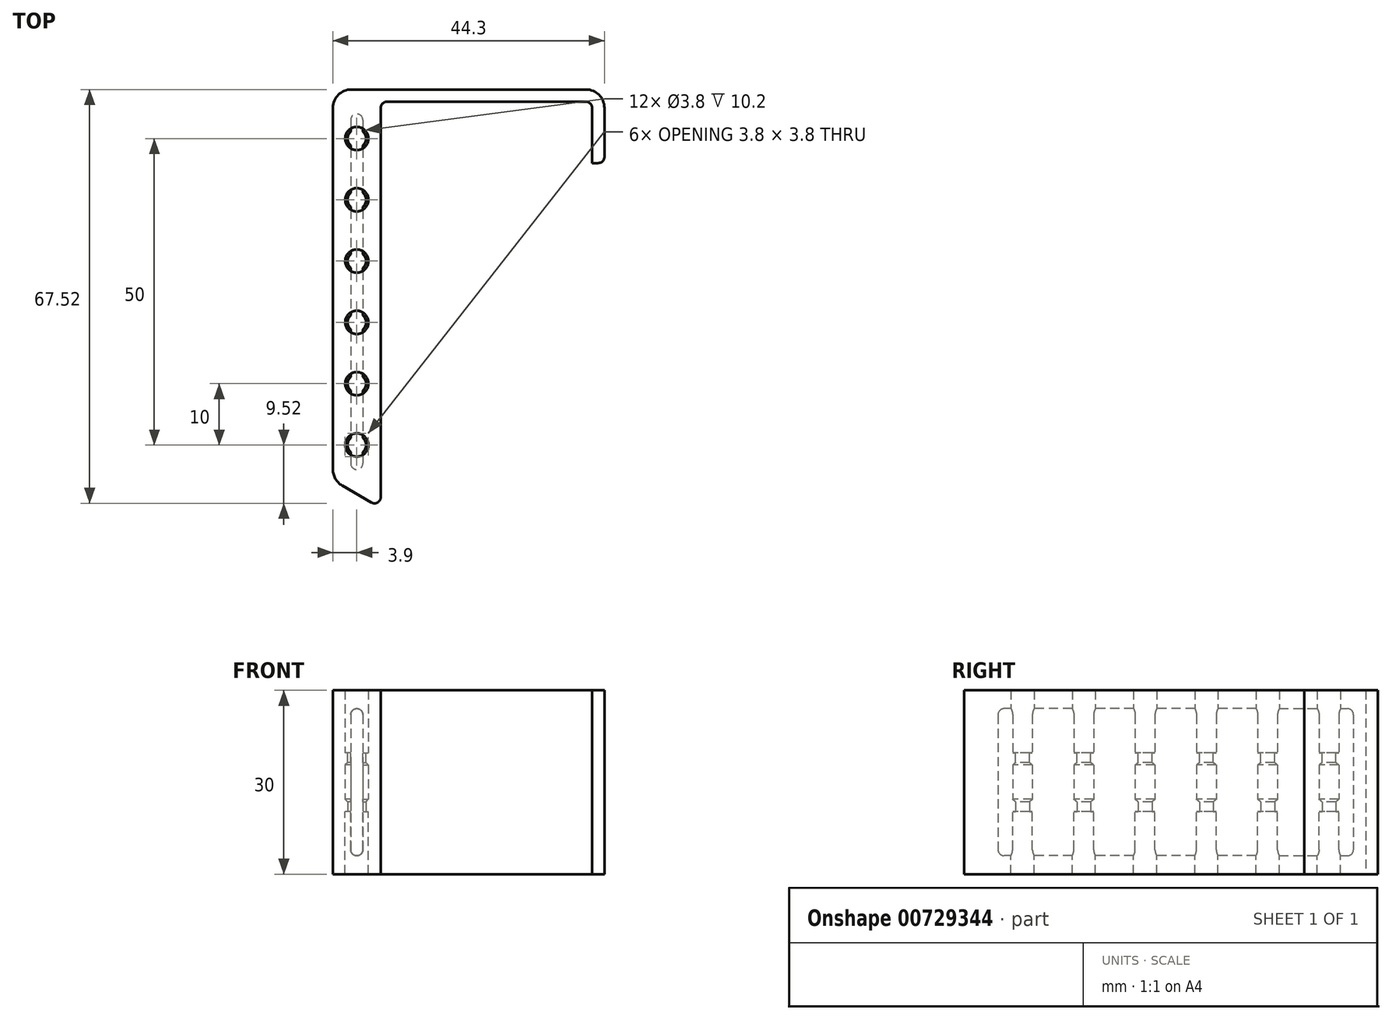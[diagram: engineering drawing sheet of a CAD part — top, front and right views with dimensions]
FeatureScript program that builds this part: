
annotation { "Feature Type Name" : "Feature", "Feature Type Description" : "" }
export const myFeature = defineFeature(function(context is Context, id is Id, definition is map)
    precondition{}
    {
        {
            var Q0;
            Q0=qCreatedBy(makeId("Top.planeOp"),FACE);
            var sketch = newSketch(context, id + "F0", { "sketchPlane" : qUnion([Q0])});
            skLineSegment(sketch, "E0", {"start": v(0, 0) * mm, "end": v(34.5, 0) * mm});
            skLineSegment(sketch, "E1", {"start": v(34.5, 0) * mm, "end": v(34.5, -10) * mm});
            skLineSegment(sketch, "E2", {"start": v(34.5, -10) * mm, "end": v(36.5, -10) * mm});
            skLineSegment(sketch, "E3", {"start": v(36.5, -10) * mm, "end": v(36.5, 2) * mm});
            skLineSegment(sketch, "E4", {"start": v(36.5, 2) * mm, "end": v(-2, 2) * mm});
            skLineSegment(sketch, "E5", {"start": v(0, 0) * mm, "end": v(0, 2) * mm, "construction": true});
            skLineSegment(sketch, "E6", {"start": v(0, 0) * mm, "end": v(-2, 0) * mm, "construction": true});
            skLineSegment(sketch, "E7", {"start": v(0, 0) * mm, "end": v(-2, 2) * mm});
            skLineSegment(sketch, "E8", {"start": v(-2, 0) * mm, "end": v(-2, 2) * mm, "construction": true});
            skSolve(sketch);
        }
        {
            var Q0;
            Q0 = qSketchRegion(id + "F0", true);
            extrude(context, id + "F1", {"entities" : qUnion([Q0]), "depth" : 15 * mm, "offsetDistance" : 25 * mm});
        }
        {
            var Q0;
            Q0=qCreatedBy(makeId("Top.planeOp"),FACE);
            var sketch = newSketch(context, id + "F2", { "sketchPlane" : qUnion([Q0])});
            skLineSegment(sketch, "E9", {"start": v(-2, 2) * mm, "end": v(-7.8, 2) * mm});
            skLineSegment(sketch, "E10", {"start": v(-7.8, 2) * mm, "end": v(-7.8, -61.75) * mm});
            skLineSegment(sketch, "E11", {"start": v(-7.8, -61.75) * mm, "end": v(0, -66.25) * mm});
            skLineSegment(sketch, "E12", {"start": v(0, -66.25) * mm, "end": v(0, 0) * mm});
            skLineSegment(sketch, "E13", {"start": v(-3.9, 2) * mm, "end": v(-3.9, -6) * mm, "construction": true});
            skLineSegment(sketch, "E14", {"start": v(-3.9, -6) * mm, "end": v(-3.9, -16) * mm, "construction": true});
            skLineSegment(sketch, "E15", {"start": v(-3.9, -16) * mm, "end": v(-3.9, -26) * mm, "construction": true});
            skLineSegment(sketch, "E16", {"start": v(-3.9, -26) * mm, "end": v(-3.9, -36) * mm, "construction": true});
            skLineSegment(sketch, "E17", {"start": v(-3.9, -36) * mm, "end": v(-3.9, -46) * mm, "construction": true});
            skLineSegment(sketch, "E18", {"start": v(-3.9, -46) * mm, "end": v(-3.9, -56) * mm, "construction": true});
            skLineSegment(sketch, "E19", {"start": v(-3.9, -56) * mm, "end": v(-3.9, -64) * mm, "construction": true});
            skCircle(sketch, "E20", {"center": v(-3.9, -6) * mm, "radius": 1.9 * mm});
            skCircle(sketch, "E21", {"center": v(-3.9, -16) * mm, "radius": 1.9 * mm});
            skCircle(sketch, "E22", {"center": v(-3.9, -26) * mm, "radius": 1.9 * mm});
            skCircle(sketch, "E23", {"center": v(-3.9, -36) * mm, "radius": 1.9 * mm});
            skCircle(sketch, "E24", {"center": v(-3.9, -46) * mm, "radius": 1.9 * mm});
            skCircle(sketch, "E25", {"center": v(-3.9, -56) * mm, "radius": 1.9 * mm});
            skLineSegment(sketch, "E26", {"start": v(-2, -56) * mm, "end": v(0, -56) * mm, "construction": true});
            skLineSegment(sketch, "E27", {"start": v(-5.8, -56) * mm, "end": v(-7.8, -56) * mm, "construction": true});
            skLineSegment(sketch, "E28", {"start": v(-2, 2) * mm, "end": v(0, 0) * mm});
            skPoint(sketch, "E29.orphan", {"position": v(0, 2) * mm});
            skSolve(sketch);
        }
        {
            var Q0;
            Q0 = qSketchRegion(id + "F2", true);
            var Q1;
            Q1=makeQuery(id+"F1.opExtrude","CAP_FACE",FACE,{"disambiguationData":[OSD([sQuery(id+"F0.wireOp",EDGE,"E0"),sQuery(id+"F0.wireOp",EDGE,"E1"),sQuery(id+"F0.wireOp",EDGE,"E2"),sQuery(id+"F0.wireOp",EDGE,"E3"),sQuery(id+"F0.wireOp",EDGE,"E4"),sQuery(id+"F0.wireOp",EDGE,"YZuL8Zb7-Wqwv-IhHu-uYE8-zltIC9lL77bN"),sQuery(id+"F0.wireOp",EDGE,"ZwzGtUW0-Jcxg-k5Jw-SNz7-18NdNkJmYsfR"),sQuery(id+"F0.wireOp",EDGE,"XFt9ytuQ-fa2W-s6oK-lxsI-mpyMaxMMDPJW")])],"isStart":false});
            extrude(context, id + "F3", {"entities" : qUnion([Q0]), "operationType" : NewBodyOperationType.ADD, "endBound" : BoundingType.UP_TO_SURFACE, "depth" : 25 * mm, "endBoundEntityFace" : qUnion([Q1]), "offsetDistance" : 25 * mm});
        }
        {
            var Q0;
            Q0=makeQuery(id+"F1.opExtrude","SWEPT_EDGE",EDGE,{"disambiguationData":[OSD([sQuery(id+"F0.wireOp",EDGE,"E0"),sQuery(id+"F0.wireOp",EDGE,"ZwzGtUW0-Jcxg-k5Jw-SNz7-18NdNkJmYsfR")])]});
            var Q1;
            Q1=makeQuery(id+"F1.opExtrude","SWEPT_EDGE",EDGE,{"disambiguationData":[OSD([sQuery(id+"F0.wireOp",EDGE,"E0"),sQuery(id+"F0.wireOp",EDGE,"E1")])]});
            var Q2;
            Q2=makeQuery(id+"F3.opExtrude","SWEPT_EDGE",EDGE,{"disambiguationData":[OSD([sQuery(id+"F2.wireOp",EDGE,"E11"),sQuery(id+"F2.wireOp",EDGE,"E12")])]});
            var Q3;
            Q3=makeQuery(id+"F1.opExtrude","SWEPT_EDGE",EDGE,{"disambiguationData":[OSD([sQuery(id+"F0.wireOp",EDGE,"E2"),sQuery(id+"F0.wireOp",EDGE,"E3")])]});
            fillet(context, id + "F4", {"entities" : qUnion([Q0, Q1, Q2, Q3]), "radius" : 1 * mm, "tangentPropagation" : true, "allowEdgeOverflow" : false});
        }
        {
            var Q0;
            Q0=makeQuery(id+"F1.opExtrude","SWEPT_EDGE",EDGE,{"disambiguationData":[OSD([sQuery(id+"F0.wireOp",EDGE,"E3"),sQuery(id+"F0.wireOp",EDGE,"E4")])]});
            var Q1;
            Q1=makeQuery(id+"F1.opExtrude","SWEPT_EDGE",EDGE,{"disambiguationData":[OSD([sQuery(id+"F0.wireOp",EDGE,"E4"),sQuery(id+"F0.wireOp",EDGE,"YZuL8Zb7-Wqwv-IhHu-uYE8-zltIC9lL77bN")])]});
            var Q2;
            Q2=makeQuery(id+"F1.opExtrude","SWEPT_EDGE",EDGE,{"disambiguationData":[OSD([sQuery(id+"F0.wireOp",EDGE,"YZuL8Zb7-Wqwv-IhHu-uYE8-zltIC9lL77bN"),sQuery(id+"F0.wireOp",EDGE,"XFt9ytuQ-fa2W-s6oK-lxsI-mpyMaxMMDPJW")])]});
            var Q3;
            Q3=makeQuery(id+"F3.opExtrude","SWEPT_EDGE",EDGE,{"disambiguationData":[OSD([sQuery(id+"F2.wireOp",EDGE,"E9"),sQuery(id+"F2.wireOp",EDGE,"E10")])]});
            var Q4;
            Q4=makeQuery(id+"F3.opExtrude","SWEPT_EDGE",EDGE,{"disambiguationData":[OSD([sQuery(id+"F2.wireOp",EDGE,"E10"),sQuery(id+"F2.wireOp",EDGE,"E11")])]});
            fillet(context, id + "F5", {"entities" : qUnion([Q0, Q1, Q2, Q3, Q4]), "radius" : 3 * mm, "tangentPropagation" : true, "allowEdgeOverflow" : false});
        }
        {
            var Q0;
            Q0=makeQuery(id+"F3.boolean.opBoolean","MERGE",FACE,{"derivedFrom":[makeQuery(id+"F1.opExtrude","CAP_FACE",FACE,{"disambiguationData":[OSD([sQuery(id+"F0.wireOp",EDGE,"E0"),sQuery(id+"F0.wireOp",EDGE,"E1"),sQuery(id+"F0.wireOp",EDGE,"E2"),sQuery(id+"F0.wireOp",EDGE,"E3"),sQuery(id+"F0.wireOp",EDGE,"E4"),sQuery(id+"F0.wireOp",EDGE,"E7")])],"isStart":false}),makeQuery(id+"F3.opExtrude","CAP_FACE",FACE,{"disambiguationData":[OSD([sQuery(id+"F2.wireOp",EDGE,"E9"),sQuery(id+"F2.wireOp",EDGE,"E10"),sQuery(id+"F2.wireOp",EDGE,"E11"),sQuery(id+"F2.wireOp",EDGE,"E12"),sQuery(id+"F2.wireOp",EDGE,"E20"),sQuery(id+"F2.wireOp",EDGE,"E21"),sQuery(id+"F2.wireOp",EDGE,"E22"),sQuery(id+"F2.wireOp",EDGE,"E23"),sQuery(id+"F2.wireOp",EDGE,"E24"),sQuery(id+"F2.wireOp",EDGE,"E25"),sQuery(id+"F2.wireOp",EDGE,"E28")])],"isStart":false})]});
            cPlane(context, id + "F6", {"entities" : qUnion([Q0]), "cplaneType" : CPlaneType.OFFSET, "offset" : 10.2 * mm, "oppositeDirection" : true, "width" : 150 * mm, "height" : 150 * mm});
        }
        {
            var Q0;
            Q0=qCreatedBy(id+"F6.planeOp",FACE);
            var sketch = newSketch(context, id + "F7", { "sketchPlane" : qUnion([Q0])});
            skCircle(sketch, "E30.0", {"center": v(-3.9, -6) * mm, "radius": 1.9 * mm});
            skCircle(sketch, "E30.1", {"center": v(-3.9, -16) * mm, "radius": 1.9 * mm});
            skCircle(sketch, "E30.2", {"center": v(-3.9, -26) * mm, "radius": 1.9 * mm});
            skCircle(sketch, "E30.3", {"center": v(-3.9, -36) * mm, "radius": 1.9 * mm});
            skCircle(sketch, "E30.4", {"center": v(-3.9, -46) * mm, "radius": 1.9 * mm});
            skCircle(sketch, "E30.5", {"center": v(-3.9, -56) * mm, "radius": 1.9 * mm});
            skCircle(sketch, "E31.0", {"center": v(-3.9, -6) * mm, "radius": 1.5 * mm});
            skCircle(sketch, "E32.0", {"center": v(-3.9, -16) * mm, "radius": 1.5 * mm});
            skCircle(sketch, "E33.0", {"center": v(-3.9, -26) * mm, "radius": 1.5 * mm});
            skCircle(sketch, "E34.0", {"center": v(-3.9, -36) * mm, "radius": 1.5 * mm});
            skCircle(sketch, "E35.0", {"center": v(-3.9, -46) * mm, "radius": 1.5 * mm});
            skCircle(sketch, "E36.0", {"center": v(-3.9, -56) * mm, "radius": 1.5 * mm});
            skSolve(sketch);
        }
        {
            var Q0;
            Q0 = qSketchRegion(id + "F7", true);
            extrude(context, id + "F8", {"entities" : qUnion([Q0]), "operationType" : NewBodyOperationType.ADD, "oppositeDirection" : true, "depth" : 1.6 * mm, "offsetDistance" : 25 * mm});
        }
        {
            var Q0;
            Q0=makeQuery(id+"F3.boolean.opBoolean","MERGE",FACE,{"derivedFrom":[makeQuery(id+"F1.opExtrude","CAP_FACE",FACE,{"disambiguationData":[OSD([sQuery(id+"F0.wireOp",EDGE,"E0"),sQuery(id+"F0.wireOp",EDGE,"E1"),sQuery(id+"F0.wireOp",EDGE,"E2"),sQuery(id+"F0.wireOp",EDGE,"E3"),sQuery(id+"F0.wireOp",EDGE,"E4"),sQuery(id+"F0.wireOp",EDGE,"E7")])],"isStart":true}),makeQuery(id+"F3.opExtrude","CAP_FACE",FACE,{"disambiguationData":[OSD([sQuery(id+"F2.wireOp",EDGE,"E9"),sQuery(id+"F2.wireOp",EDGE,"E10"),sQuery(id+"F2.wireOp",EDGE,"E11"),sQuery(id+"F2.wireOp",EDGE,"E12"),sQuery(id+"F2.wireOp",EDGE,"E20"),sQuery(id+"F2.wireOp",EDGE,"E21"),sQuery(id+"F2.wireOp",EDGE,"E22"),sQuery(id+"F2.wireOp",EDGE,"E23"),sQuery(id+"F2.wireOp",EDGE,"E24"),sQuery(id+"F2.wireOp",EDGE,"E25"),sQuery(id+"F2.wireOp",EDGE,"E28")])],"isStart":true})]});
            var sketch = newSketch(context, id + "F9", { "sketchPlane" : qUnion([Q0])});
            skLineSegment(sketch, "E37.bottom", {"start": v(-2.9, 2) * mm, "end": v(-4.9, 2) * mm});
            skLineSegment(sketch, "E37.top", {"start": v(-2.9, 60) * mm, "end": v(-4.9, 60) * mm});
            skLineSegment(sketch, "E37.left", {"start": v(-2.9, 2) * mm, "end": v(-2.9, 60) * mm});
            skLineSegment(sketch, "E37.right", {"start": v(-4.9, 2) * mm, "end": v(-4.9, 60) * mm});
            skLineSegment(sketch, "E38", {"start": v(-3.9, 2) * mm, "end": v(-3.9, 6) * mm, "construction": true});
            skLineSegment(sketch, "E39", {"start": v(-3.9, 6) * mm, "end": v(-3.9, 56) * mm, "construction": true});
            skLineSegment(sketch, "E40", {"start": v(-3.9, 56) * mm, "end": v(-3.9, 60) * mm, "construction": true});
            skSolve(sketch);
        }
        {
            var Q0;
            Q0 = qSketchRegion(id + "F9", true);
            var Q1;
            Q1=makeQuery(id+"F3.boolean.opBoolean","MERGE",FACE,{"derivedFrom":[makeQuery(id+"F1.opExtrude","CAP_FACE",FACE,{"disambiguationData":[OSD([sQuery(id+"F0.wireOp",EDGE,"E0"),sQuery(id+"F0.wireOp",EDGE,"E1"),sQuery(id+"F0.wireOp",EDGE,"E2"),sQuery(id+"F0.wireOp",EDGE,"E3"),sQuery(id+"F0.wireOp",EDGE,"E4"),sQuery(id+"F0.wireOp",EDGE,"E7")])],"isStart":false}),makeQuery(id+"F3.opExtrude","CAP_FACE",FACE,{"disambiguationData":[OSD([sQuery(id+"F2.wireOp",EDGE,"E9"),sQuery(id+"F2.wireOp",EDGE,"E10"),sQuery(id+"F2.wireOp",EDGE,"E11"),sQuery(id+"F2.wireOp",EDGE,"E12"),sQuery(id+"F2.wireOp",EDGE,"E20"),sQuery(id+"F2.wireOp",EDGE,"E21"),sQuery(id+"F2.wireOp",EDGE,"E22"),sQuery(id+"F2.wireOp",EDGE,"E23"),sQuery(id+"F2.wireOp",EDGE,"E24"),sQuery(id+"F2.wireOp",EDGE,"E25"),sQuery(id+"F2.wireOp",EDGE,"E28")])],"isStart":false})]});
            extrude(context, id + "F10", {"entities" : qUnion([Q0]), "operationType" : NewBodyOperationType.REMOVE, "endBound" : BoundingType.UP_TO_SURFACE, "oppositeDirection" : true, "depth" : 25 * mm, "endBoundEntityFace" : qUnion([Q1]), "hasOffset" : true, "offsetDistance" : 3 * mm});
        }
        {
            var Q0;
            Q0=makeQuery(id+"F10.boolean.opBoolean","COPY",EDGE,{"derivedFrom":makeQuery(id+"F10.opExtrude","SWEPT_EDGE",EDGE,{"disambiguationData":[OSD([sQuery(id+"F9.wireOp",EDGE,"E37.bottom"),sQuery(id+"F9.wireOp",EDGE,"E37.left")])]})});
            var Q1;
            Q1=makeQuery(id+"F10.boolean.opBoolean","COPY",EDGE,{"derivedFrom":makeQuery(id+"F10.opExtrude","SWEPT_EDGE",EDGE,{"disambiguationData":[OSD([sQuery(id+"F9.wireOp",EDGE,"E37.bottom"),sQuery(id+"F9.wireOp",EDGE,"E37.right")])]})});
            var Q2;
            {var subQ0=sQuery(id+"F9.wireOp",EDGE,"E37.bottom");var subQ1=sQuery(id+"F9.wireOp",EDGE,"E37.right");Q2=makeQuery(id+"F10.boolean.opBoolean","COPY",EDGE,{"disambiguationData":[TD([makeQuery(id+"F3.opExtrude","SWEPT_FACE",FACE,{"disambiguationData":[OSD([sQuery(id+"F2.wireOp",EDGE,"E20")])]}),makeQuery(id+"F10.opExtrude","SWEPT_FACE",FACE,{"disambiguationData":[OSD([subQ0])]}),makeQuery(id+"F10.opExtrude","CAP_FACE",FACE,{"disambiguationData":[OSD([subQ0,sQuery(id+"F9.wireOp",EDGE,"E37.top"),sQuery(id+"F9.wireOp",EDGE,"E37.left"),subQ1])],"isStart":false}),makeQuery(id+"F10.opExtrude","SWEPT_FACE",FACE,{"disambiguationData":[OSD([subQ1])]})])],"derivedFrom":makeQuery(id+"F10.opExtrude","CAP_EDGE",EDGE,{"disambiguationData":[OSD([subQ1])],"isStart":false})});}
            var Q3;
            {var subQ0=sQuery(id+"F9.wireOp",EDGE,"E37.bottom");var subQ1=sQuery(id+"F9.wireOp",EDGE,"E37.left");Q3=makeQuery(id+"F10.boolean.opBoolean","COPY",EDGE,{"disambiguationData":[TD([makeQuery(id+"F3.opExtrude","SWEPT_FACE",FACE,{"disambiguationData":[OSD([sQuery(id+"F2.wireOp",EDGE,"E20")])]}),makeQuery(id+"F10.opExtrude","SWEPT_FACE",FACE,{"disambiguationData":[OSD([subQ0])]}),makeQuery(id+"F10.opExtrude","CAP_FACE",FACE,{"disambiguationData":[OSD([subQ0,sQuery(id+"F9.wireOp",EDGE,"E37.top"),subQ1,sQuery(id+"F9.wireOp",EDGE,"E37.right")])],"isStart":false}),makeQuery(id+"F10.opExtrude","SWEPT_FACE",FACE,{"disambiguationData":[OSD([subQ1])]})])],"derivedFrom":makeQuery(id+"F10.opExtrude","CAP_EDGE",EDGE,{"disambiguationData":[OSD([subQ1])],"isStart":false})});}
            var Q4;
            {var subQ0=sQuery(id+"F9.wireOp",EDGE,"E37.left");Q4=makeQuery(id+"F10.boolean.opBoolean","COPY",EDGE,{"disambiguationData":[TD([makeQuery(id+"F3.opExtrude","SWEPT_FACE",FACE,{"disambiguationData":[OSD([sQuery(id+"F2.wireOp",EDGE,"E20")])]}),makeQuery(id+"F3.opExtrude","SWEPT_FACE",FACE,{"disambiguationData":[OSD([sQuery(id+"F2.wireOp",EDGE,"E21")])]}),makeQuery(id+"F10.opExtrude","CAP_FACE",FACE,{"disambiguationData":[OSD([sQuery(id+"F9.wireOp",EDGE,"E37.bottom"),sQuery(id+"F9.wireOp",EDGE,"E37.top"),subQ0,sQuery(id+"F9.wireOp",EDGE,"E37.right")])],"isStart":false}),makeQuery(id+"F10.opExtrude","SWEPT_FACE",FACE,{"disambiguationData":[OSD([subQ0])]})])],"derivedFrom":makeQuery(id+"F10.opExtrude","CAP_EDGE",EDGE,{"disambiguationData":[OSD([subQ0])],"isStart":false})});}
            var Q5;
            {var subQ0=sQuery(id+"F9.wireOp",EDGE,"E37.right");Q5=makeQuery(id+"F10.boolean.opBoolean","COPY",EDGE,{"disambiguationData":[TD([makeQuery(id+"F3.opExtrude","SWEPT_FACE",FACE,{"disambiguationData":[OSD([sQuery(id+"F2.wireOp",EDGE,"E20")])]}),makeQuery(id+"F3.opExtrude","SWEPT_FACE",FACE,{"disambiguationData":[OSD([sQuery(id+"F2.wireOp",EDGE,"E21")])]}),makeQuery(id+"F10.opExtrude","CAP_FACE",FACE,{"disambiguationData":[OSD([sQuery(id+"F9.wireOp",EDGE,"E37.bottom"),sQuery(id+"F9.wireOp",EDGE,"E37.top"),sQuery(id+"F9.wireOp",EDGE,"E37.left"),subQ0])],"isStart":false}),makeQuery(id+"F10.opExtrude","SWEPT_FACE",FACE,{"disambiguationData":[OSD([subQ0])]})])],"derivedFrom":makeQuery(id+"F10.opExtrude","CAP_EDGE",EDGE,{"disambiguationData":[OSD([subQ0])],"isStart":false})});}
            var Q6;
            {var subQ0=sQuery(id+"F9.wireOp",EDGE,"E37.right");Q6=makeQuery(id+"F10.boolean.opBoolean","COPY",EDGE,{"disambiguationData":[TD([makeQuery(id+"F3.opExtrude","SWEPT_FACE",FACE,{"disambiguationData":[OSD([sQuery(id+"F2.wireOp",EDGE,"E21")])]}),makeQuery(id+"F3.opExtrude","SWEPT_FACE",FACE,{"disambiguationData":[OSD([sQuery(id+"F2.wireOp",EDGE,"E22")])]}),makeQuery(id+"F10.opExtrude","CAP_FACE",FACE,{"disambiguationData":[OSD([sQuery(id+"F9.wireOp",EDGE,"E37.bottom"),sQuery(id+"F9.wireOp",EDGE,"E37.top"),sQuery(id+"F9.wireOp",EDGE,"E37.left"),subQ0])],"isStart":false}),makeQuery(id+"F10.opExtrude","SWEPT_FACE",FACE,{"disambiguationData":[OSD([subQ0])]})])],"derivedFrom":makeQuery(id+"F10.opExtrude","CAP_EDGE",EDGE,{"disambiguationData":[OSD([subQ0])],"isStart":false})});}
            var Q7;
            {var subQ0=sQuery(id+"F9.wireOp",EDGE,"E37.right");Q7=makeQuery(id+"F10.boolean.opBoolean","COPY",EDGE,{"disambiguationData":[TD([makeQuery(id+"F3.opExtrude","SWEPT_FACE",FACE,{"disambiguationData":[OSD([sQuery(id+"F2.wireOp",EDGE,"E22")])]}),makeQuery(id+"F3.opExtrude","SWEPT_FACE",FACE,{"disambiguationData":[OSD([sQuery(id+"F2.wireOp",EDGE,"E23")])]}),makeQuery(id+"F10.opExtrude","CAP_FACE",FACE,{"disambiguationData":[OSD([sQuery(id+"F9.wireOp",EDGE,"E37.bottom"),sQuery(id+"F9.wireOp",EDGE,"E37.top"),sQuery(id+"F9.wireOp",EDGE,"E37.left"),subQ0])],"isStart":false}),makeQuery(id+"F10.opExtrude","SWEPT_FACE",FACE,{"disambiguationData":[OSD([subQ0])]})])],"derivedFrom":makeQuery(id+"F10.opExtrude","CAP_EDGE",EDGE,{"disambiguationData":[OSD([subQ0])],"isStart":false})});}
            var Q8;
            {var subQ0=sQuery(id+"F9.wireOp",EDGE,"E37.right");Q8=makeQuery(id+"F10.boolean.opBoolean","COPY",EDGE,{"disambiguationData":[TD([makeQuery(id+"F3.opExtrude","SWEPT_FACE",FACE,{"disambiguationData":[OSD([sQuery(id+"F2.wireOp",EDGE,"E23")])]}),makeQuery(id+"F3.opExtrude","SWEPT_FACE",FACE,{"disambiguationData":[OSD([sQuery(id+"F2.wireOp",EDGE,"E24")])]}),makeQuery(id+"F10.opExtrude","CAP_FACE",FACE,{"disambiguationData":[OSD([sQuery(id+"F9.wireOp",EDGE,"E37.bottom"),sQuery(id+"F9.wireOp",EDGE,"E37.top"),sQuery(id+"F9.wireOp",EDGE,"E37.left"),subQ0])],"isStart":false}),makeQuery(id+"F10.opExtrude","SWEPT_FACE",FACE,{"disambiguationData":[OSD([subQ0])]})])],"derivedFrom":makeQuery(id+"F10.opExtrude","CAP_EDGE",EDGE,{"disambiguationData":[OSD([subQ0])],"isStart":false})});}
            var Q9;
            {var subQ0=sQuery(id+"F9.wireOp",EDGE,"E37.right");Q9=makeQuery(id+"F10.boolean.opBoolean","COPY",EDGE,{"disambiguationData":[TD([makeQuery(id+"F3.opExtrude","SWEPT_FACE",FACE,{"disambiguationData":[OSD([sQuery(id+"F2.wireOp",EDGE,"E24")])]}),makeQuery(id+"F3.opExtrude","SWEPT_FACE",FACE,{"disambiguationData":[OSD([sQuery(id+"F2.wireOp",EDGE,"E25")])]}),makeQuery(id+"F10.opExtrude","CAP_FACE",FACE,{"disambiguationData":[OSD([sQuery(id+"F9.wireOp",EDGE,"E37.bottom"),sQuery(id+"F9.wireOp",EDGE,"E37.top"),sQuery(id+"F9.wireOp",EDGE,"E37.left"),subQ0])],"isStart":false}),makeQuery(id+"F10.opExtrude","SWEPT_FACE",FACE,{"disambiguationData":[OSD([subQ0])]})])],"derivedFrom":makeQuery(id+"F10.opExtrude","CAP_EDGE",EDGE,{"disambiguationData":[OSD([subQ0])],"isStart":false})});}
            var Q10;
            {var subQ0=sQuery(id+"F9.wireOp",EDGE,"E37.right");var subQ1=sQuery(id+"F9.wireOp",EDGE,"E37.top");Q10=makeQuery(id+"F10.boolean.opBoolean","COPY",EDGE,{"disambiguationData":[TD([makeQuery(id+"F3.opExtrude","SWEPT_FACE",FACE,{"disambiguationData":[OSD([sQuery(id+"F2.wireOp",EDGE,"E25")])]}),makeQuery(id+"F10.opExtrude","CAP_FACE",FACE,{"disambiguationData":[OSD([sQuery(id+"F9.wireOp",EDGE,"E37.bottom"),subQ1,sQuery(id+"F9.wireOp",EDGE,"E37.left"),subQ0])],"isStart":false}),makeQuery(id+"F10.opExtrude","SWEPT_FACE",FACE,{"disambiguationData":[OSD([subQ1])]}),makeQuery(id+"F10.opExtrude","SWEPT_FACE",FACE,{"disambiguationData":[OSD([subQ0])]})])],"derivedFrom":makeQuery(id+"F10.opExtrude","CAP_EDGE",EDGE,{"disambiguationData":[OSD([subQ0])],"isStart":false})});}
            var Q11;
            Q11=makeQuery(id+"F10.boolean.opBoolean","COPY",EDGE,{"derivedFrom":makeQuery(id+"F10.opExtrude","SWEPT_EDGE",EDGE,{"disambiguationData":[OSD([sQuery(id+"F9.wireOp",EDGE,"E37.top"),sQuery(id+"F9.wireOp",EDGE,"E37.right")])]})});
            var Q12;
            Q12=makeQuery(id+"F10.boolean.opBoolean","COPY",EDGE,{"derivedFrom":makeQuery(id+"F10.opExtrude","CAP_EDGE",EDGE,{"disambiguationData":[OSD([sQuery(id+"F9.wireOp",EDGE,"E37.top")])],"isStart":false})});
            var Q13;
            {var subQ0=sQuery(id+"F9.wireOp",EDGE,"E37.left");var subQ1=sQuery(id+"F9.wireOp",EDGE,"E37.top");Q13=makeQuery(id+"F10.boolean.opBoolean","COPY",EDGE,{"disambiguationData":[TD([makeQuery(id+"F3.opExtrude","SWEPT_FACE",FACE,{"disambiguationData":[OSD([sQuery(id+"F2.wireOp",EDGE,"E25")])]}),makeQuery(id+"F10.opExtrude","CAP_FACE",FACE,{"disambiguationData":[OSD([sQuery(id+"F9.wireOp",EDGE,"E37.bottom"),subQ1,subQ0,sQuery(id+"F9.wireOp",EDGE,"E37.right")])],"isStart":false}),makeQuery(id+"F10.opExtrude","SWEPT_FACE",FACE,{"disambiguationData":[OSD([subQ1])]}),makeQuery(id+"F10.opExtrude","SWEPT_FACE",FACE,{"disambiguationData":[OSD([subQ0])]})])],"derivedFrom":makeQuery(id+"F10.opExtrude","CAP_EDGE",EDGE,{"disambiguationData":[OSD([subQ0])],"isStart":false})});}
            var Q14;
            Q14=makeQuery(id+"F10.boolean.opBoolean","COPY",EDGE,{"derivedFrom":makeQuery(id+"F10.opExtrude","SWEPT_EDGE",EDGE,{"disambiguationData":[OSD([sQuery(id+"F9.wireOp",EDGE,"E37.top"),sQuery(id+"F9.wireOp",EDGE,"E37.left")])]})});
            var Q15;
            {var subQ0=sQuery(id+"F9.wireOp",EDGE,"E37.left");Q15=makeQuery(id+"F10.boolean.opBoolean","COPY",EDGE,{"disambiguationData":[TD([makeQuery(id+"F3.opExtrude","SWEPT_FACE",FACE,{"disambiguationData":[OSD([sQuery(id+"F2.wireOp",EDGE,"E24")])]}),makeQuery(id+"F3.opExtrude","SWEPT_FACE",FACE,{"disambiguationData":[OSD([sQuery(id+"F2.wireOp",EDGE,"E25")])]}),makeQuery(id+"F10.opExtrude","CAP_FACE",FACE,{"disambiguationData":[OSD([sQuery(id+"F9.wireOp",EDGE,"E37.bottom"),sQuery(id+"F9.wireOp",EDGE,"E37.top"),subQ0,sQuery(id+"F9.wireOp",EDGE,"E37.right")])],"isStart":false}),makeQuery(id+"F10.opExtrude","SWEPT_FACE",FACE,{"disambiguationData":[OSD([subQ0])]})])],"derivedFrom":makeQuery(id+"F10.opExtrude","CAP_EDGE",EDGE,{"disambiguationData":[OSD([subQ0])],"isStart":false})});}
            var Q16;
            {var subQ0=sQuery(id+"F9.wireOp",EDGE,"E37.left");Q16=makeQuery(id+"F10.boolean.opBoolean","COPY",EDGE,{"disambiguationData":[TD([makeQuery(id+"F3.opExtrude","SWEPT_FACE",FACE,{"disambiguationData":[OSD([sQuery(id+"F2.wireOp",EDGE,"E23")])]}),makeQuery(id+"F3.opExtrude","SWEPT_FACE",FACE,{"disambiguationData":[OSD([sQuery(id+"F2.wireOp",EDGE,"E24")])]}),makeQuery(id+"F10.opExtrude","CAP_FACE",FACE,{"disambiguationData":[OSD([sQuery(id+"F9.wireOp",EDGE,"E37.bottom"),sQuery(id+"F9.wireOp",EDGE,"E37.top"),subQ0,sQuery(id+"F9.wireOp",EDGE,"E37.right")])],"isStart":false}),makeQuery(id+"F10.opExtrude","SWEPT_FACE",FACE,{"disambiguationData":[OSD([subQ0])]})])],"derivedFrom":makeQuery(id+"F10.opExtrude","CAP_EDGE",EDGE,{"disambiguationData":[OSD([subQ0])],"isStart":false})});}
            var Q17;
            {var subQ0=sQuery(id+"F9.wireOp",EDGE,"E37.left");Q17=makeQuery(id+"F10.boolean.opBoolean","COPY",EDGE,{"disambiguationData":[TD([makeQuery(id+"F3.opExtrude","SWEPT_FACE",FACE,{"disambiguationData":[OSD([sQuery(id+"F2.wireOp",EDGE,"E22")])]}),makeQuery(id+"F3.opExtrude","SWEPT_FACE",FACE,{"disambiguationData":[OSD([sQuery(id+"F2.wireOp",EDGE,"E23")])]}),makeQuery(id+"F10.opExtrude","CAP_FACE",FACE,{"disambiguationData":[OSD([sQuery(id+"F9.wireOp",EDGE,"E37.bottom"),sQuery(id+"F9.wireOp",EDGE,"E37.top"),subQ0,sQuery(id+"F9.wireOp",EDGE,"E37.right")])],"isStart":false}),makeQuery(id+"F10.opExtrude","SWEPT_FACE",FACE,{"disambiguationData":[OSD([subQ0])]})])],"derivedFrom":makeQuery(id+"F10.opExtrude","CAP_EDGE",EDGE,{"disambiguationData":[OSD([subQ0])],"isStart":false})});}
            var Q18;
            {var subQ0=sQuery(id+"F9.wireOp",EDGE,"E37.left");Q18=makeQuery(id+"F10.boolean.opBoolean","COPY",EDGE,{"disambiguationData":[TD([makeQuery(id+"F3.opExtrude","SWEPT_FACE",FACE,{"disambiguationData":[OSD([sQuery(id+"F2.wireOp",EDGE,"E21")])]}),makeQuery(id+"F3.opExtrude","SWEPT_FACE",FACE,{"disambiguationData":[OSD([sQuery(id+"F2.wireOp",EDGE,"E22")])]}),makeQuery(id+"F10.opExtrude","CAP_FACE",FACE,{"disambiguationData":[OSD([sQuery(id+"F9.wireOp",EDGE,"E37.bottom"),sQuery(id+"F9.wireOp",EDGE,"E37.top"),subQ0,sQuery(id+"F9.wireOp",EDGE,"E37.right")])],"isStart":false}),makeQuery(id+"F10.opExtrude","SWEPT_FACE",FACE,{"disambiguationData":[OSD([subQ0])]})])],"derivedFrom":makeQuery(id+"F10.opExtrude","CAP_EDGE",EDGE,{"disambiguationData":[OSD([subQ0])],"isStart":false})});}
            var Q19;
            Q19=makeQuery(id+"F10.boolean.opBoolean","COPY",EDGE,{"derivedFrom":makeQuery(id+"F10.opExtrude","CAP_EDGE",EDGE,{"disambiguationData":[OSD([sQuery(id+"F9.wireOp",EDGE,"E37.bottom")])],"isStart":false})});
            fillet(context, id + "F11", {"entities" : qUnion([Q0, Q1, Q2, Q3, Q4, Q5, Q6, Q7, Q8, Q9, Q10, Q11, Q12, Q13, Q14, Q15, Q16, Q17, Q18, Q19]), "radius" : 1 * mm, "tangentPropagation" : true, "allowEdgeOverflow" : false});
        }
        {
            var Q0;
            {var subQ0=sQuery(id+"F7.wireOp",EDGE,"E30.0");Q0=makeQuery(id+"F10.boolean.opBoolean","SPLIT",EDGE,{"disambiguationData":[TD([makeQuery(id+"F10.opExtrude","SWEPT_FACE",FACE,{"disambiguationData":[OSD([sQuery(id+"F9.wireOp",EDGE,"E37.left")])]})])],"derivedFrom":makeQuery(id+"F8.opExtrude","CAP_EDGE",EDGE,{"disambiguationData":[OSD([subQ0])],"isStart":false})});}
            var Q1;
            {var subQ0=sQuery(id+"F7.wireOp",EDGE,"E30.1");Q1=makeQuery(id+"F10.boolean.opBoolean","SPLIT",EDGE,{"disambiguationData":[TD([makeQuery(id+"F10.opExtrude","SWEPT_FACE",FACE,{"disambiguationData":[OSD([sQuery(id+"F9.wireOp",EDGE,"E37.left")])]})])],"derivedFrom":makeQuery(id+"F8.opExtrude","CAP_EDGE",EDGE,{"disambiguationData":[OSD([subQ0])],"isStart":false})});}
            var Q2;
            {var subQ0=sQuery(id+"F7.wireOp",EDGE,"E30.2");Q2=makeQuery(id+"F10.boolean.opBoolean","SPLIT",EDGE,{"disambiguationData":[TD([makeQuery(id+"F10.opExtrude","SWEPT_FACE",FACE,{"disambiguationData":[OSD([sQuery(id+"F9.wireOp",EDGE,"E37.left")])]})])],"derivedFrom":makeQuery(id+"F8.opExtrude","CAP_EDGE",EDGE,{"disambiguationData":[OSD([subQ0])],"isStart":false})});}
            var Q3;
            {var subQ0=sQuery(id+"F7.wireOp",EDGE,"E30.3");Q3=makeQuery(id+"F10.boolean.opBoolean","SPLIT",EDGE,{"disambiguationData":[TD([makeQuery(id+"F10.opExtrude","SWEPT_FACE",FACE,{"disambiguationData":[OSD([sQuery(id+"F9.wireOp",EDGE,"E37.left")])]})])],"derivedFrom":makeQuery(id+"F8.opExtrude","CAP_EDGE",EDGE,{"disambiguationData":[OSD([subQ0])],"isStart":false})});}
            var Q4;
            {var subQ0=sQuery(id+"F7.wireOp",EDGE,"E30.4");Q4=makeQuery(id+"F10.boolean.opBoolean","SPLIT",EDGE,{"disambiguationData":[TD([makeQuery(id+"F10.opExtrude","SWEPT_FACE",FACE,{"disambiguationData":[OSD([sQuery(id+"F9.wireOp",EDGE,"E37.left")])]})])],"derivedFrom":makeQuery(id+"F8.opExtrude","CAP_EDGE",EDGE,{"disambiguationData":[OSD([subQ0])],"isStart":false})});}
            var Q5;
            {var subQ0=sQuery(id+"F7.wireOp",EDGE,"E30.5");Q5=makeQuery(id+"F10.boolean.opBoolean","SPLIT",EDGE,{"disambiguationData":[TD([makeQuery(id+"F10.opExtrude","SWEPT_FACE",FACE,{"disambiguationData":[OSD([sQuery(id+"F9.wireOp",EDGE,"E37.left")])]})])],"derivedFrom":makeQuery(id+"F8.opExtrude","CAP_EDGE",EDGE,{"disambiguationData":[OSD([subQ0])],"isStart":false})});}
            var Q6;
            {var subQ0=sQuery(id+"F7.wireOp",EDGE,"E30.5");Q6=makeQuery(id+"F10.boolean.opBoolean","SPLIT",EDGE,{"disambiguationData":[TD([makeQuery(id+"F10.opExtrude","SWEPT_FACE",FACE,{"disambiguationData":[OSD([sQuery(id+"F9.wireOp",EDGE,"E37.right")])]})])],"derivedFrom":makeQuery(id+"F8.opExtrude","CAP_EDGE",EDGE,{"disambiguationData":[OSD([subQ0])],"isStart":false})});}
            var Q7;
            {var subQ0=sQuery(id+"F7.wireOp",EDGE,"E30.4");Q7=makeQuery(id+"F10.boolean.opBoolean","SPLIT",EDGE,{"disambiguationData":[TD([makeQuery(id+"F10.opExtrude","SWEPT_FACE",FACE,{"disambiguationData":[OSD([sQuery(id+"F9.wireOp",EDGE,"E37.right")])]})])],"derivedFrom":makeQuery(id+"F8.opExtrude","CAP_EDGE",EDGE,{"disambiguationData":[OSD([subQ0])],"isStart":false})});}
            var Q8;
            {var subQ0=sQuery(id+"F7.wireOp",EDGE,"E30.3");Q8=makeQuery(id+"F10.boolean.opBoolean","SPLIT",EDGE,{"disambiguationData":[TD([makeQuery(id+"F10.opExtrude","SWEPT_FACE",FACE,{"disambiguationData":[OSD([sQuery(id+"F9.wireOp",EDGE,"E37.right")])]})])],"derivedFrom":makeQuery(id+"F8.opExtrude","CAP_EDGE",EDGE,{"disambiguationData":[OSD([subQ0])],"isStart":false})});}
            var Q9;
            {var subQ0=sQuery(id+"F7.wireOp",EDGE,"E30.2");Q9=makeQuery(id+"F10.boolean.opBoolean","SPLIT",EDGE,{"disambiguationData":[TD([makeQuery(id+"F10.opExtrude","SWEPT_FACE",FACE,{"disambiguationData":[OSD([sQuery(id+"F9.wireOp",EDGE,"E37.right")])]})])],"derivedFrom":makeQuery(id+"F8.opExtrude","CAP_EDGE",EDGE,{"disambiguationData":[OSD([subQ0])],"isStart":false})});}
            var Q10;
            {var subQ0=sQuery(id+"F7.wireOp",EDGE,"E30.1");Q10=makeQuery(id+"F10.boolean.opBoolean","SPLIT",EDGE,{"disambiguationData":[TD([makeQuery(id+"F10.opExtrude","SWEPT_FACE",FACE,{"disambiguationData":[OSD([sQuery(id+"F9.wireOp",EDGE,"E37.right")])]})])],"derivedFrom":makeQuery(id+"F8.opExtrude","CAP_EDGE",EDGE,{"disambiguationData":[OSD([subQ0])],"isStart":false})});}
            var Q11;
            {var subQ0=sQuery(id+"F7.wireOp",EDGE,"E30.0");Q11=makeQuery(id+"F10.boolean.opBoolean","SPLIT",EDGE,{"disambiguationData":[TD([makeQuery(id+"F10.opExtrude","SWEPT_FACE",FACE,{"disambiguationData":[OSD([sQuery(id+"F9.wireOp",EDGE,"E37.right")])]})])],"derivedFrom":makeQuery(id+"F8.opExtrude","CAP_EDGE",EDGE,{"disambiguationData":[OSD([subQ0])],"isStart":false})});}
            var Q12;
            {var subQ0=sQuery(id+"F7.wireOp",EDGE,"E30.0");Q12=makeQuery(id+"F10.boolean.opBoolean","SPLIT",EDGE,{"disambiguationData":[TD([makeQuery(id+"F10.opExtrude","SWEPT_FACE",FACE,{"disambiguationData":[OSD([sQuery(id+"F9.wireOp",EDGE,"E37.right")])]})])],"derivedFrom":makeQuery(id+"F8.opExtrude","CAP_EDGE",EDGE,{"disambiguationData":[OSD([subQ0])],"isStart":true})});}
            var Q13;
            {var subQ0=sQuery(id+"F7.wireOp",EDGE,"E30.0");Q13=makeQuery(id+"F10.boolean.opBoolean","SPLIT",EDGE,{"disambiguationData":[TD([makeQuery(id+"F10.opExtrude","SWEPT_FACE",FACE,{"disambiguationData":[OSD([sQuery(id+"F9.wireOp",EDGE,"E37.left")])]})])],"derivedFrom":makeQuery(id+"F8.opExtrude","CAP_EDGE",EDGE,{"disambiguationData":[OSD([subQ0])],"isStart":true})});}
            var Q14;
            {var subQ0=sQuery(id+"F7.wireOp",EDGE,"E30.1");Q14=makeQuery(id+"F10.boolean.opBoolean","SPLIT",EDGE,{"disambiguationData":[TD([makeQuery(id+"F10.opExtrude","SWEPT_FACE",FACE,{"disambiguationData":[OSD([sQuery(id+"F9.wireOp",EDGE,"E37.right")])]})])],"derivedFrom":makeQuery(id+"F8.opExtrude","CAP_EDGE",EDGE,{"disambiguationData":[OSD([subQ0])],"isStart":true})});}
            var Q15;
            {var subQ0=sQuery(id+"F7.wireOp",EDGE,"E30.2");Q15=makeQuery(id+"F10.boolean.opBoolean","SPLIT",EDGE,{"disambiguationData":[TD([makeQuery(id+"F10.opExtrude","SWEPT_FACE",FACE,{"disambiguationData":[OSD([sQuery(id+"F9.wireOp",EDGE,"E37.left")])]})])],"derivedFrom":makeQuery(id+"F8.opExtrude","CAP_EDGE",EDGE,{"disambiguationData":[OSD([subQ0])],"isStart":true})});}
            var Q16;
            {var subQ0=sQuery(id+"F7.wireOp",EDGE,"E30.3");Q16=makeQuery(id+"F10.boolean.opBoolean","SPLIT",EDGE,{"disambiguationData":[TD([makeQuery(id+"F10.opExtrude","SWEPT_FACE",FACE,{"disambiguationData":[OSD([sQuery(id+"F9.wireOp",EDGE,"E37.left")])]})])],"derivedFrom":makeQuery(id+"F8.opExtrude","CAP_EDGE",EDGE,{"disambiguationData":[OSD([subQ0])],"isStart":true})});}
            var Q17;
            {var subQ0=sQuery(id+"F7.wireOp",EDGE,"E30.3");Q17=makeQuery(id+"F10.boolean.opBoolean","SPLIT",EDGE,{"disambiguationData":[TD([makeQuery(id+"F10.opExtrude","SWEPT_FACE",FACE,{"disambiguationData":[OSD([sQuery(id+"F9.wireOp",EDGE,"E37.right")])]})])],"derivedFrom":makeQuery(id+"F8.opExtrude","CAP_EDGE",EDGE,{"disambiguationData":[OSD([subQ0])],"isStart":true})});}
            var Q18;
            {var subQ0=sQuery(id+"F7.wireOp",EDGE,"E30.4");Q18=makeQuery(id+"F10.boolean.opBoolean","SPLIT",EDGE,{"disambiguationData":[TD([makeQuery(id+"F10.opExtrude","SWEPT_FACE",FACE,{"disambiguationData":[OSD([sQuery(id+"F9.wireOp",EDGE,"E37.left")])]})])],"derivedFrom":makeQuery(id+"F8.opExtrude","CAP_EDGE",EDGE,{"disambiguationData":[OSD([subQ0])],"isStart":true})});}
            var Q19;
            {var subQ0=sQuery(id+"F7.wireOp",EDGE,"E30.5");Q19=makeQuery(id+"F10.boolean.opBoolean","SPLIT",EDGE,{"disambiguationData":[TD([makeQuery(id+"F10.opExtrude","SWEPT_FACE",FACE,{"disambiguationData":[OSD([sQuery(id+"F9.wireOp",EDGE,"E37.right")])]})])],"derivedFrom":makeQuery(id+"F8.opExtrude","CAP_EDGE",EDGE,{"disambiguationData":[OSD([subQ0])],"isStart":true})});}
            var Q20;
            {var subQ0=sQuery(id+"F7.wireOp",EDGE,"E30.5");Q20=makeQuery(id+"F10.boolean.opBoolean","SPLIT",EDGE,{"disambiguationData":[TD([makeQuery(id+"F10.opExtrude","SWEPT_FACE",FACE,{"disambiguationData":[OSD([sQuery(id+"F9.wireOp",EDGE,"E37.left")])]})])],"derivedFrom":makeQuery(id+"F8.opExtrude","CAP_EDGE",EDGE,{"disambiguationData":[OSD([subQ0])],"isStart":true})});}
            var Q21;
            {var subQ0=sQuery(id+"F7.wireOp",EDGE,"E30.4");Q21=makeQuery(id+"F10.boolean.opBoolean","SPLIT",EDGE,{"disambiguationData":[TD([makeQuery(id+"F10.opExtrude","SWEPT_FACE",FACE,{"disambiguationData":[OSD([sQuery(id+"F9.wireOp",EDGE,"E37.right")])]})])],"derivedFrom":makeQuery(id+"F8.opExtrude","CAP_EDGE",EDGE,{"disambiguationData":[OSD([subQ0])],"isStart":true})});}
            var Q22;
            {var subQ0=sQuery(id+"F7.wireOp",EDGE,"E30.2");Q22=makeQuery(id+"F10.boolean.opBoolean","SPLIT",EDGE,{"disambiguationData":[TD([makeQuery(id+"F10.opExtrude","SWEPT_FACE",FACE,{"disambiguationData":[OSD([sQuery(id+"F9.wireOp",EDGE,"E37.right")])]})])],"derivedFrom":makeQuery(id+"F8.opExtrude","CAP_EDGE",EDGE,{"disambiguationData":[OSD([subQ0])],"isStart":true})});}
            var Q23;
            {var subQ0=sQuery(id+"F7.wireOp",EDGE,"E30.1");Q23=makeQuery(id+"F10.boolean.opBoolean","SPLIT",EDGE,{"disambiguationData":[TD([makeQuery(id+"F10.opExtrude","SWEPT_FACE",FACE,{"disambiguationData":[OSD([sQuery(id+"F9.wireOp",EDGE,"E37.left")])]})])],"derivedFrom":makeQuery(id+"F8.opExtrude","CAP_EDGE",EDGE,{"disambiguationData":[OSD([subQ0])],"isStart":true})});}
            chamfer(context, id + "F12", {"entities" : qUnion([Q0, Q1, Q2, Q3, Q4, Q5, Q6, Q7, Q8, Q9, Q10, Q11, Q12, Q13, Q14, Q15, Q16, Q17, Q18, Q19, Q20, Q21, Q22, Q23]), "width" : .4 * mm, "tangentPropagation" : true});
        }
        {
            var Q0;
            Q0=makeQuery(id+"F1.opExtrude","SWEPT_BODY",BODY,{"disambiguationData":[OSD([sQuery(id+"F0.wireOp",EDGE,"E0"),sQuery(id+"F0.wireOp",EDGE,"E1"),sQuery(id+"F0.wireOp",EDGE,"E2"),sQuery(id+"F0.wireOp",EDGE,"E3"),sQuery(id+"F0.wireOp",EDGE,"E4"),sQuery(id+"F0.wireOp",EDGE,"E7")])]});
            var Q1;
            Q1=makeQuery(id+"F3.boolean.opBoolean","MERGE",FACE,{"derivedFrom":[makeQuery(id+"F1.opExtrude","CAP_FACE",FACE,{"disambiguationData":[OSD([sQuery(id+"F0.wireOp",EDGE,"E0"),sQuery(id+"F0.wireOp",EDGE,"E1"),sQuery(id+"F0.wireOp",EDGE,"E2"),sQuery(id+"F0.wireOp",EDGE,"E3"),sQuery(id+"F0.wireOp",EDGE,"E4"),sQuery(id+"F0.wireOp",EDGE,"E7")])],"isStart":true}),makeQuery(id+"F3.opExtrude","CAP_FACE",FACE,{"disambiguationData":[OSD([sQuery(id+"F2.wireOp",EDGE,"E9"),sQuery(id+"F2.wireOp",EDGE,"E10"),sQuery(id+"F2.wireOp",EDGE,"E11"),sQuery(id+"F2.wireOp",EDGE,"E12"),sQuery(id+"F2.wireOp",EDGE,"E20"),sQuery(id+"F2.wireOp",EDGE,"E21"),sQuery(id+"F2.wireOp",EDGE,"E22"),sQuery(id+"F2.wireOp",EDGE,"E23"),sQuery(id+"F2.wireOp",EDGE,"E24"),sQuery(id+"F2.wireOp",EDGE,"E25"),sQuery(id+"F2.wireOp",EDGE,"E28")])],"isStart":true})]});
            mirror(context, id + "F13", {"operationType" : NewBodyOperationType.ADD, "entities" : qUnion([Q0]), "mirrorPlane" : qUnion([Q1])});
        }
    });
